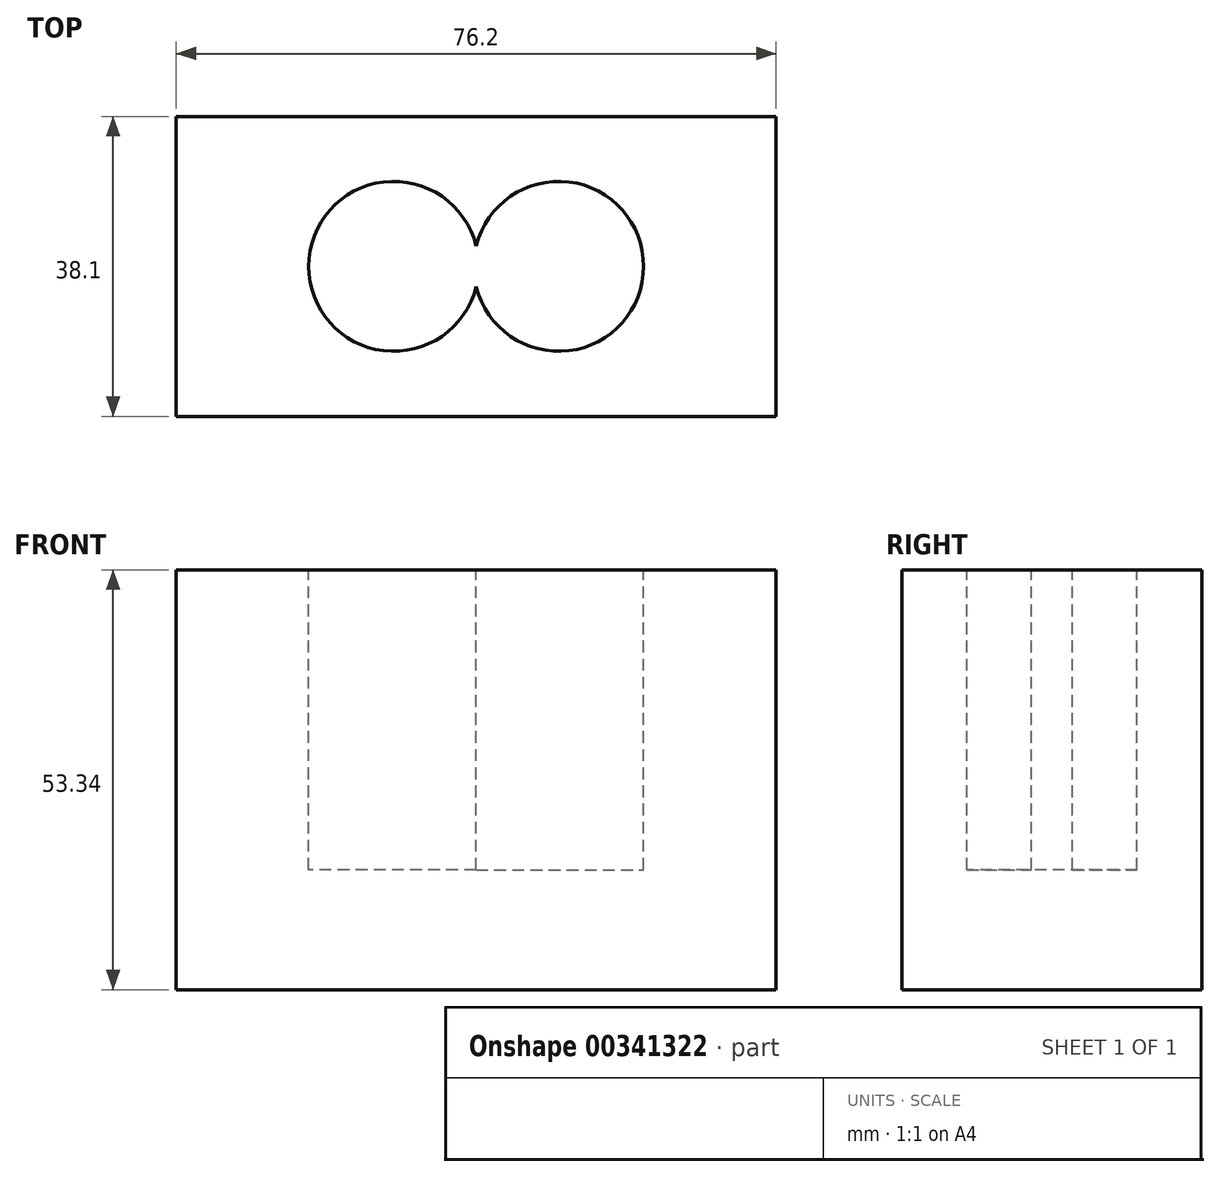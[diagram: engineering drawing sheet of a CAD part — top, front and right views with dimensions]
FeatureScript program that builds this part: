
annotation { "Feature Type Name" : "Feature", "Feature Type Description" : "" }
export const myFeature = defineFeature(function(context is Context, id is Id, definition is map)
    precondition{}
    {
        {
            var Q0;
            Q0=qCreatedBy(makeId("Top.planeOp"),FACE);
            var sketch = newSketch(context, id + "F0", { "sketchPlane" : qUnion([Q0])});
            skLineSegment(sketch, "E0.bottom", {"start": v(38.1, 19.05) * mm, "end": v(-38.1, 19.05) * mm});
            skLineSegment(sketch, "E0.top", {"start": v(38.1, -19.05) * mm, "end": v(-38.1, -19.05) * mm});
            skLineSegment(sketch, "E0.left", {"start": v(38.1, 19.05) * mm, "end": v(38.1, -19.05) * mm});
            skLineSegment(sketch, "E0.right", {"start": v(-38.1, 19.05) * mm, "end": v(-38.1, -19.05) * mm});
            skPoint(sketch, "E0.middle", {"position": v(0, 0) * mm});
            skSolve(sketch);
        }
        {
            var Q0;
            Q0 = qSketchRegion(id + "F0", true);
            extrude(context, id + "F1", {"entities" : qUnion([Q0]), "depth" : 53.34 * mm});
        }
        {
            var Q0;
            Q0=makeQuery(id+"F1.opExtrude","CAP_FACE",FACE,{"disambiguationData":[OSD([sQuery(id+"F0.wireOp",EDGE,"E0.bottom"),sQuery(id+"F0.wireOp",EDGE,"E0.top"),sQuery(id+"F0.wireOp",EDGE,"E0.left"),sQuery(id+"F0.wireOp",EDGE,"E0.right")])],"isStart":false});
            var sketch = newSketch(context, id + "F2", { "sketchPlane" : qUnion([Q0])});
            skCircle(sketch, "E1", {"center": v(-10.48, 0) * mm, "radius": 10.8 * mm});
            skCircle(sketch, "E2", {"center": v(10.48, 0) * mm, "radius": 10.8 * mm});
            skSolve(sketch);
        }
        {
            var Q0;
            Q0 = qSketchRegion(id + "F2", true);
            extrude(context, id + "F3", {"entities" : qUnion([Q0]), "operationType" : NewBodyOperationType.REMOVE, "oppositeDirection" : true, "depth" : 38.1 * mm});
        }
    });
